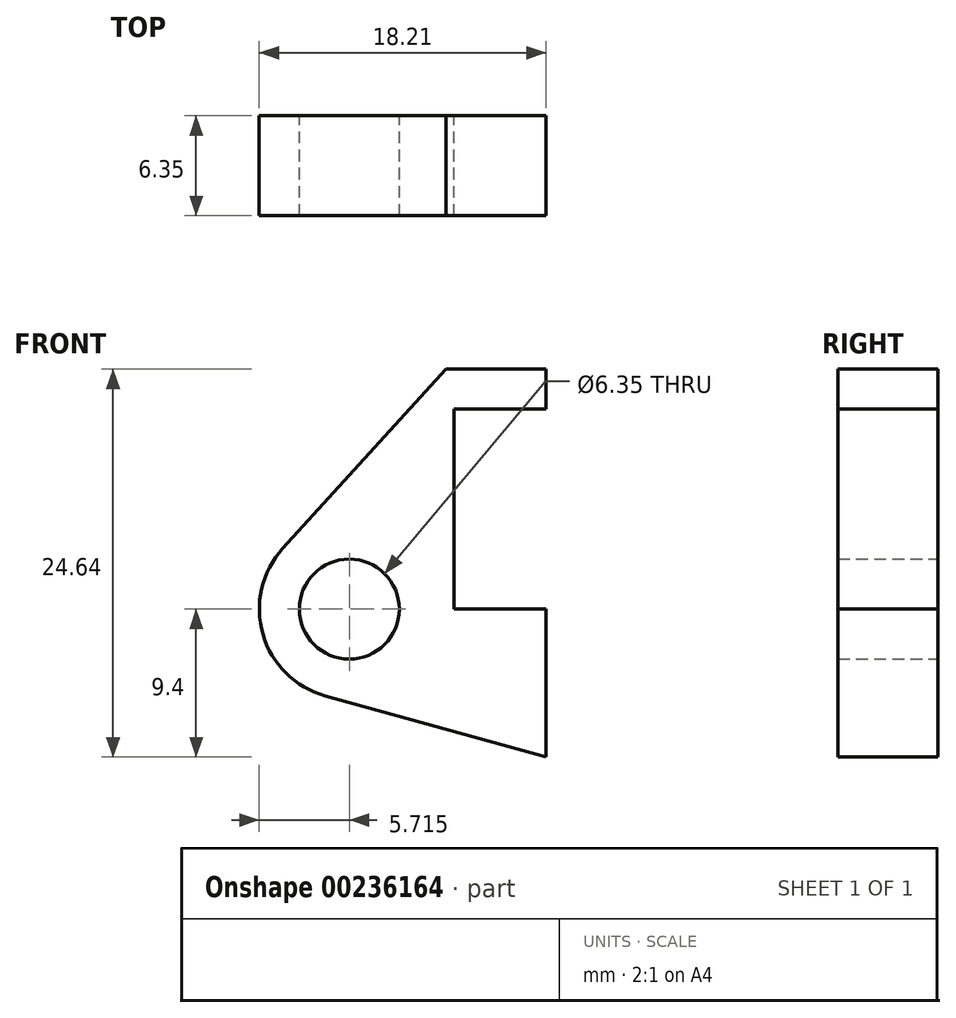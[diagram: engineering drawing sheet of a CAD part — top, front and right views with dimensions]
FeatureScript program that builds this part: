
annotation { "Feature Type Name" : "Feature", "Feature Type Description" : "" }
export const myFeature = defineFeature(function(context is Context, id is Id, definition is map)
    precondition{}
    {
        {
            var Q0;
            Q0=qCreatedBy(makeId("Front.planeOp"),FACE);
            var sketch = newSketch(context, id + "F0", { "sketchPlane" : qUnion([Q0])});
            skLineSegment(sketch, "E0", {"start": v(0, 0) * mm, "end": v(0, 12.7) * mm});
            skLineSegment(sketch, "E1", {"start": v(0, 12.7) * mm, "end": v(10.16, 12.7) * mm});
            skLineSegment(sketch, "E2", {"start": v(10.16, 12.7) * mm, "end": v(10.16, 10.16) * mm});
            skLineSegment(sketch, "E3", {"start": v(10.16, 10.16) * mm, "end": v(56.13, 10.16) * mm});
            skLineSegment(sketch, "E4", {"start": v(56.13, 10.16) * mm, "end": v(56.13, 12.7) * mm});
            skLineSegment(sketch, "E5", {"start": v(56.13, 12.7) * mm, "end": v(66.3, 12.7) * mm});
            skLineSegment(sketch, "E6", {"start": v(66.3, 12.7) * mm, "end": v(66.3, 0) * mm});
            skLineSegment(sketch, "E7", {"start": v(66.3, 0) * mm, "end": v(0, 0) * mm});
            skLineSegment(sketch, "E8", {"start": v(5.84, 15.24) * mm, "end": v(-0.5, 15.24) * mm});
            skLineSegment(sketch, "E9", {"start": v(-0.5, 15.24) * mm, "end": v(-10.88, 3.85) * mm});
            skLineSegment(sketch, "E10", {"start": v(0, 0) * mm, "end": v(-6.65, 0) * mm});
            skCircle(sketch, "E11", {"center": v(-6.65, 0) * mm, "radius": 5.72 * mm});
            skCircle(sketch, "E12", {"center": v(-6.65, 0) * mm, "radius": 3.18 * mm});
            skLineSegment(sketch, "E13", {"start": v(5.84, 15.24) * mm, "end": v(5.84, -9.4) * mm});
            skLineSegment(sketch, "E14", {"start": v(5.84, -9.4) * mm, "end": v(-8.18, -5.5) * mm});
            skSolve(sketch);
        }
        {
            var Q0;
            {var subQ3=sQuery(id+"F0.wireOp",EDGE,"E0");Q0=makeQuery(id+"F0.imprint","IMPRINT",FACE,{"disambiguationData":[TD([[makeQuery(id+"F0.imprint","IMPRINT",EDGE,{"derivedFrom":subQ3}),1.0]])]});}
            var Q1;
            {var subQ0=sQuery(id+"F0.wireOp",EDGE,"E14");Q1=makeQuery(id+"F0.imprint","IMPRINT",FACE,{"disambiguationData":[TD([[makeQuery(id+"F0.imprint","IMPRINT",EDGE,{"derivedFrom":subQ0}),-1.0]])]});}
            var Q2;
            {var subQ4=sQuery(id+"F0.wireOp",EDGE,"E12");Q2=makeQuery(id+"F0.imprint","IMPRINT",FACE,{"disambiguationData":[TD([[makeQuery(id+"F0.imprint","IMPRINT",EDGE,{"derivedFrom":subQ4}),-1.0]])]});}
            extrude(context, id + "F1", {"entities" : qUnion([Q0, Q1, Q2]), "depth" : 6.35 * mm});
        }
    });
